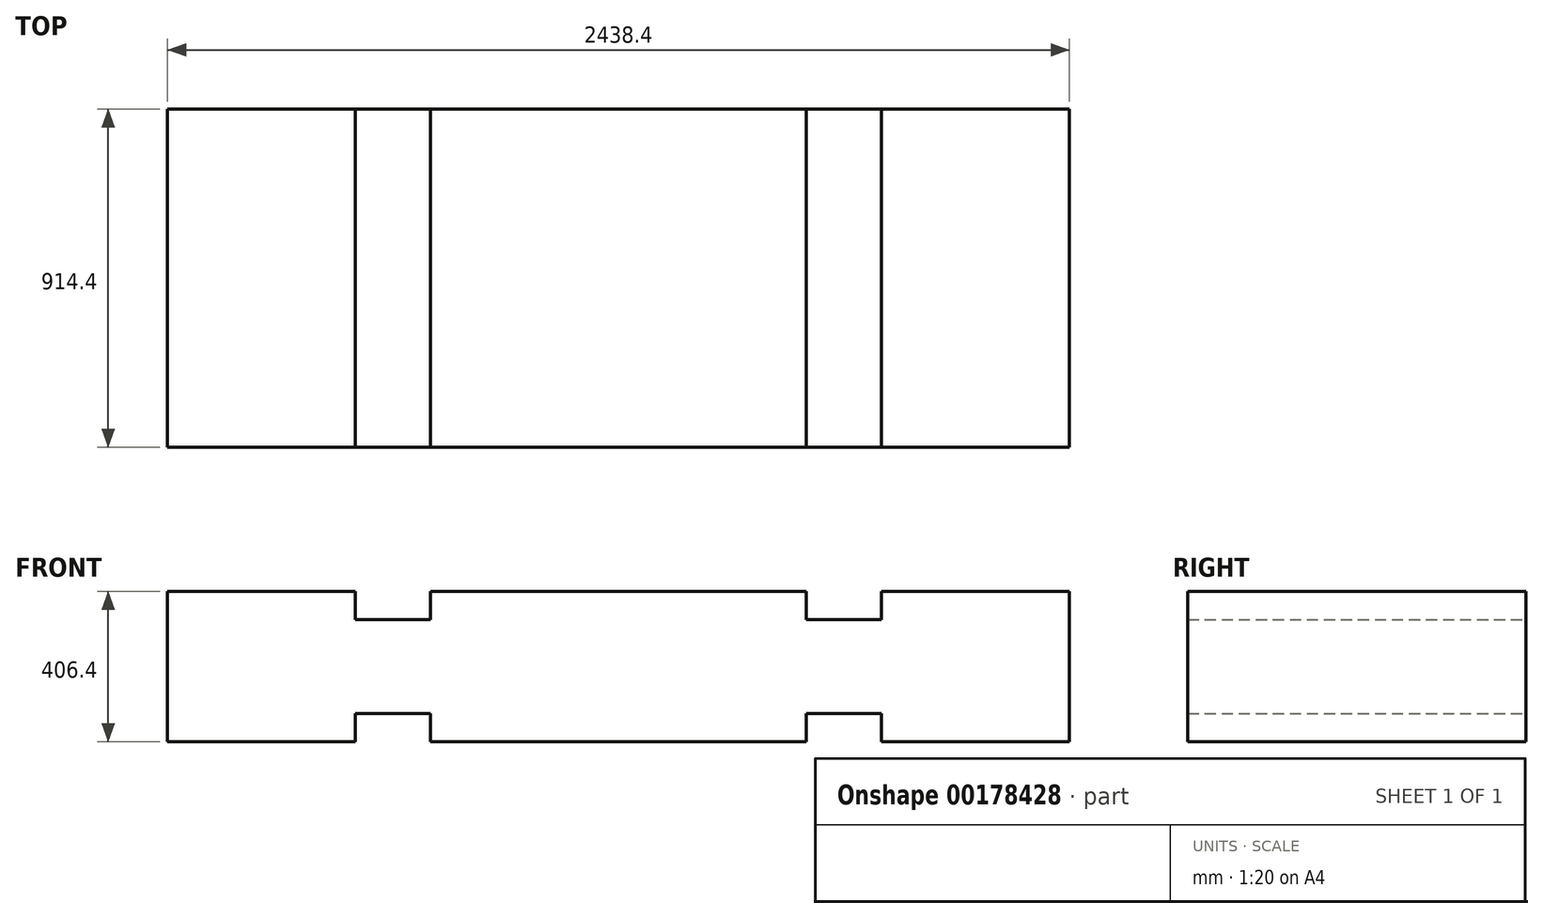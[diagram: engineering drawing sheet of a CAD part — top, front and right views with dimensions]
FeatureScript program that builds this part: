
annotation { "Feature Type Name" : "Feature", "Feature Type Description" : "" }
export const myFeature = defineFeature(function(context is Context, id is Id, definition is map)
    precondition{}
    {
        {
            var Q0;
            Q0=qCreatedBy(makeId("Front.planeOp"),FACE);
            var sketch = newSketch(context, id + "F0", { "sketchPlane" : qUnion([Q0])});
            skLineSegment(sketch, "E0.bottom", {"start": v(-1219.2, 203.2) * mm, "end": v(1219.2, 203.2) * mm});
            skLineSegment(sketch, "E0.top", {"start": v(-1219.2, -203.2) * mm, "end": v(1219.2, -203.2) * mm});
            skLineSegment(sketch, "E0.left", {"start": v(-1219.2, 203.2) * mm, "end": v(-1219.2, -203.2) * mm});
            skLineSegment(sketch, "E0.right", {"start": v(1219.2, 203.2) * mm, "end": v(1219.2, -203.2) * mm});
            skLineSegment(sketch, "E1", {"start": v(-1219.2, 203.2) * mm, "end": v(1219.2, -203.2) * mm, "construction": true});
            skLineSegment(sketch, "E2", {"start": v(-711.2, 203.2) * mm, "end": v(-711.2, 127) * mm});
            skLineSegment(sketch, "E3", {"start": v(-711.2, 127) * mm, "end": v(-508, 127) * mm});
            skLineSegment(sketch, "E4", {"start": v(-508, 127) * mm, "end": v(-508, 203.2) * mm});
            skLineSegment(sketch, "E5", {"start": v(-609.6, 127) * mm, "end": v(-609.6, 203.2) * mm, "construction": true});
            skLineSegment(sketch, "E6.MirrorCS", {"start": v(508, 127) * mm, "end": v(508, 203.2) * mm});
            skLineSegment(sketch, "E7.MirrorCS", {"start": v(711.2, 127) * mm, "end": v(508, 127) * mm});
            skLineSegment(sketch, "E8.MirrorCS", {"start": v(711.2, 203.2) * mm, "end": v(711.2, 127) * mm});
            skLineSegment(sketch, "E9.MirrorCS", {"start": v(-508, -127) * mm, "end": v(-508, -203.2) * mm});
            skLineSegment(sketch, "E10.MirrorCS", {"start": v(-711.2, -127) * mm, "end": v(-508, -127) * mm});
            skLineSegment(sketch, "E11.MirrorCS", {"start": v(-711.2, -203.2) * mm, "end": v(-711.2, -127) * mm});
            skLineSegment(sketch, "E12.MirrorCS", {"start": v(508, -127) * mm, "end": v(508, -203.2) * mm});
            skLineSegment(sketch, "E13.MirrorCS", {"start": v(711.2, -127) * mm, "end": v(508, -127) * mm});
            skLineSegment(sketch, "E14.MirrorCS", {"start": v(711.2, -203.2) * mm, "end": v(711.2, -127) * mm});
            skSolve(sketch);
        }
        {
            var Q0;
            {var subQ3=sQuery(id+"F0.wireOp",EDGE,"E0.left");Q0=makeQuery(id+"F0.imprint","IMPRINT",FACE,{"disambiguationData":[TD([[makeQuery(id+"F0.imprint","IMPRINT",EDGE,{"derivedFrom":subQ3}),1.0]])]});}
            extrude(context, id + "F1", {"entities" : qUnion([Q0]), "endBound" : BoundingType.SYMMETRIC, "depth" : 914.4 * mm});
        }
    });
